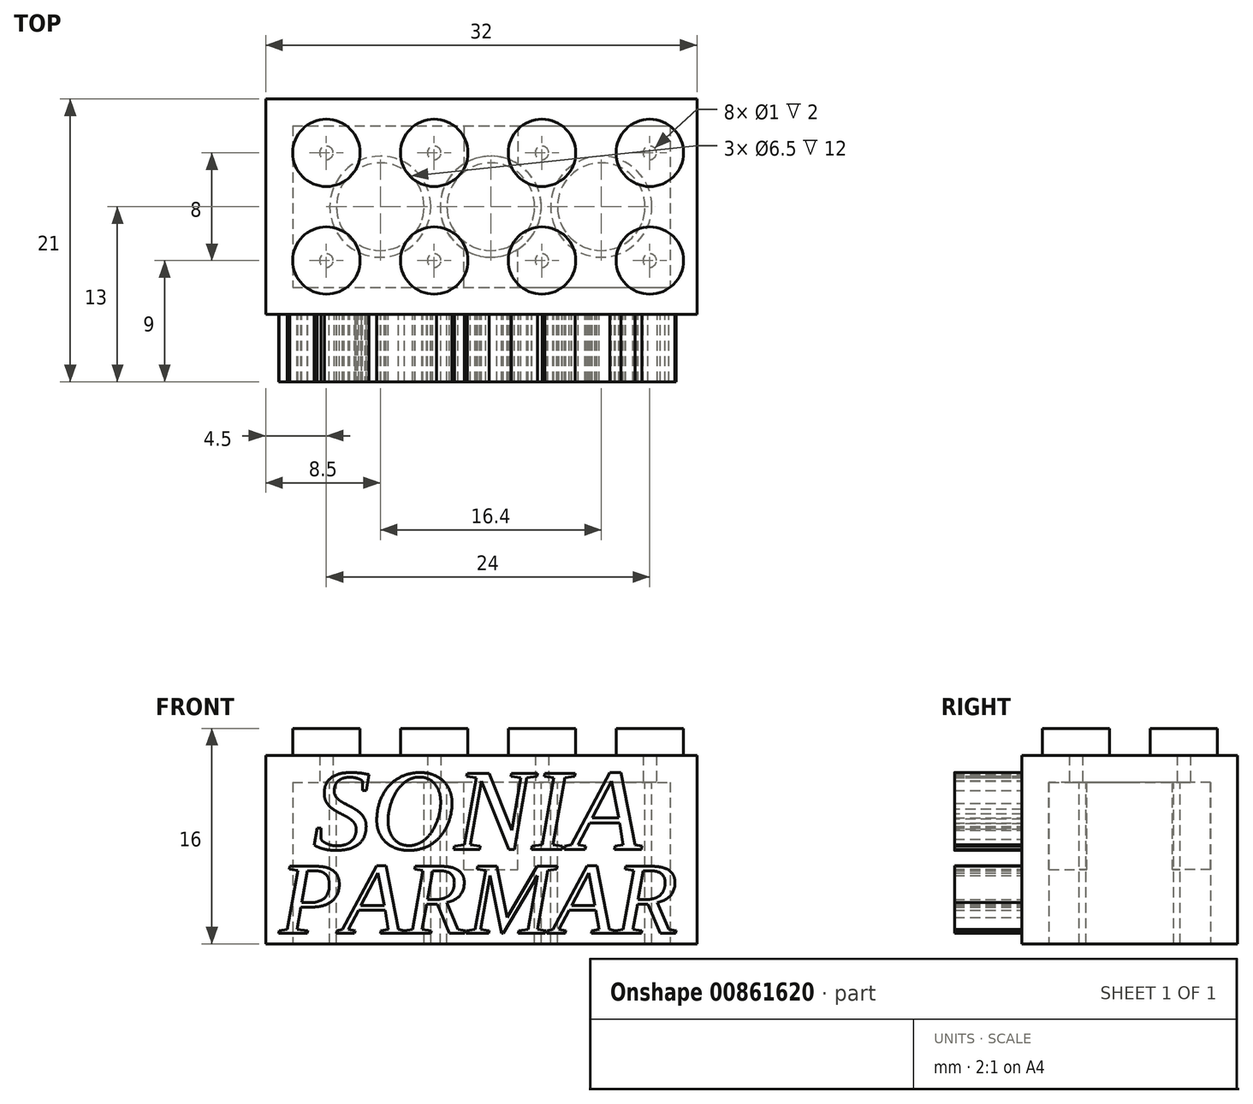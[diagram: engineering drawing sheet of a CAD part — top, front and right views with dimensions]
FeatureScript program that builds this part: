
annotation { "Feature Type Name" : "Feature", "Feature Type Description" : "" }
export const myFeature = defineFeature(function(context is Context, id is Id, definition is map)
    precondition{}
    {
        {
            var Q0;
            Q0=qCreatedBy(makeId("Top.planeOp"),FACE);
            var sketch = newSketch(context, id + "F0", { "sketchPlane" : qUnion([Q0])});
            skLineSegment(sketch, "E0.bottom", {"start": v(-16, 8) * mm, "end": v(16, 8) * mm});
            skLineSegment(sketch, "E0.top", {"start": v(-16, -8) * mm, "end": v(16, -8) * mm});
            skLineSegment(sketch, "E0.left", {"start": v(-16, 8) * mm, "end": v(-16, -8) * mm});
            skLineSegment(sketch, "E0.right", {"start": v(16, 8) * mm, "end": v(16, -8) * mm});
            skPoint(sketch, "E1", {"position": v(-16, 0) * mm});
            skPoint(sketch, "E2", {"position": v(0, 8) * mm});
            skPoint(sketch, "E3", {"position": v(16, 0) * mm});
            skPoint(sketch, "E4", {"position": v(0, -8) * mm});
            skPoint(sketch, "E5", {"position": v(0, 0) * mm});
            skSolve(sketch);
        }
        {
            var Q0;
            Q0=makeQuery(id+"F0.imprint","IMPRINT",FACE,{"disambiguationData":[TD([[makeQuery(id+"F0.imprint","IMPRINT",EDGE,{"derivedFrom":sQuery(id+"F0.wireOp",EDGE,"E0.bottom")}),-1.0]])]});
            extrude(context, id + "F1", {"entities" : qUnion([Q0]), "depth" : 14 * mm, "offsetDistance" : 25 * mm});
        }
        {
            var Q0;
            Q0=makeQuery(id+"F1.opExtrude","CAP_FACE",FACE,{"disambiguationData":[OSD([sQuery(id+"F0.wireOp",EDGE,"E0.bottom"),sQuery(id+"F0.wireOp",EDGE,"E0.top"),sQuery(id+"F0.wireOp",EDGE,"E0.left"),sQuery(id+"F0.wireOp",EDGE,"E0.right")])],"isStart":false});
            var sketch = newSketch(context, id + "F2", { "sketchPlane" : qUnion([Q0])});
            skCircle(sketch, "E6", {"center": v(-11.5, 4) * mm, "radius": 2.5 * mm});
            skCircle(sketch, "E7.0.1.0", {"center": v(-11.5, -4) * mm, "radius": 2.5 * mm});
            skCircle(sketch, "E7.1.0.0", {"center": v(-3.5, 4) * mm, "radius": 2.5 * mm});
            skCircle(sketch, "E7.1.1.0", {"center": v(-3.5, -4) * mm, "radius": 2.5 * mm});
            skCircle(sketch, "E7.2.0.0", {"center": v(4.5, 4) * mm, "radius": 2.5 * mm});
            skCircle(sketch, "E7.2.1.0", {"center": v(4.5, -4) * mm, "radius": 2.5 * mm});
            skCircle(sketch, "E7.3.0.0", {"center": v(12.5, 4) * mm, "radius": 2.5 * mm});
            skCircle(sketch, "E7.3.1.0", {"center": v(12.5, -4) * mm, "radius": 2.5 * mm});
            skLineSegment(sketch, "E7.direction1", {"start": v(-11.5, 4) * mm, "end": v(-3.5, 4) * mm, "construction": true});
            skLineSegment(sketch, "E7.direction2", {"start": v(-11.5, 4) * mm, "end": v(-11.5, -4) * mm, "construction": true});
            skSolve(sketch);
        }
        {
            var Q0;
            Q0=makeQuery(id+"F2.imprint","IMPRINT",FACE,{"disambiguationData":[TD([[makeQuery(id+"F2.imprint","IMPRINT",EDGE,{"derivedFrom":sQuery(id+"F2.wireOp",EDGE,"E6")}),1.0]])]});
            var Q1;
            Q1=makeQuery(id+"F2.imprint","IMPRINT",FACE,{"disambiguationData":[TD([[makeQuery(id+"F2.imprint","IMPRINT",EDGE,{"derivedFrom":sQuery(id+"F2.wireOp",EDGE,"E7.1.0.0")}),1.0]])]});
            var Q2;
            Q2=makeQuery(id+"F2.imprint","IMPRINT",FACE,{"disambiguationData":[TD([[makeQuery(id+"F2.imprint","IMPRINT",EDGE,{"derivedFrom":sQuery(id+"F2.wireOp",EDGE,"E7.3.0.0")}),1.0]])]});
            var Q3;
            Q3=makeQuery(id+"F2.imprint","IMPRINT",FACE,{"disambiguationData":[TD([[makeQuery(id+"F2.imprint","IMPRINT",EDGE,{"derivedFrom":sQuery(id+"F2.wireOp",EDGE,"E7.3.1.0")}),1.0]])]});
            var Q4;
            Q4=makeQuery(id+"F2.imprint","IMPRINT",FACE,{"disambiguationData":[TD([[makeQuery(id+"F2.imprint","IMPRINT",EDGE,{"derivedFrom":sQuery(id+"F2.wireOp",EDGE,"E7.2.1.0")}),1.0]])]});
            var Q5;
            Q5=makeQuery(id+"F2.imprint","IMPRINT",FACE,{"disambiguationData":[TD([[makeQuery(id+"F2.imprint","IMPRINT",EDGE,{"derivedFrom":sQuery(id+"F2.wireOp",EDGE,"E7.1.1.0")}),1.0]])]});
            var Q6;
            Q6=makeQuery(id+"F2.imprint","IMPRINT",FACE,{"disambiguationData":[TD([[makeQuery(id+"F2.imprint","IMPRINT",EDGE,{"derivedFrom":sQuery(id+"F2.wireOp",EDGE,"E7.0.1.0")}),1.0]])]});
            var Q7;
            Q7=makeQuery(id+"F2.imprint","IMPRINT",FACE,{"disambiguationData":[TD([[makeQuery(id+"F2.imprint","IMPRINT",EDGE,{"derivedFrom":sQuery(id+"F2.wireOp",EDGE,"E7.2.0.0")}),1.0]])]});
            extrude(context, id + "F3", {"entities" : qUnion([Q0, Q1, Q2, Q3, Q4, Q5, Q6, Q7]), "operationType" : NewBodyOperationType.ADD, "depth" : 2 * mm, "offsetDistance" : 25 * mm});
        }
        {
            var Q0;
            Q0=makeQuery(id+"F1.opExtrude","CAP_FACE",FACE,{"disambiguationData":[OSD([sQuery(id+"F0.wireOp",EDGE,"E0.bottom"),sQuery(id+"F0.wireOp",EDGE,"E0.top"),sQuery(id+"F0.wireOp",EDGE,"E0.left"),sQuery(id+"F0.wireOp",EDGE,"E0.right")])],"isStart":true});
            shell(context, id + "F4", {"entities" : qUnion([Q0]), "thickness" : 2 * mm});
        }
        {
            var Q0;
            Q0=makeQuery(id+"F4.opShell","OFFSET_FACE",FACE,{"disambiguationData":[OSD([sQuery(id+"F0.wireOp",EDGE,"E0.bottom"),sQuery(id+"F0.wireOp",EDGE,"E0.top"),sQuery(id+"F0.wireOp",EDGE,"E0.left"),sQuery(id+"F0.wireOp",EDGE,"E0.right")])]});
            var sketch = newSketch(context, id + "F5", { "sketchPlane" : qUnion([Q0])});
            skCircle(sketch, "E8", {"center": v(-7.5, 0) * mm, "radius": 3.75 * mm});
            skLineSegment(sketch, "E9", {"start": v(-11.5, 4) * mm, "end": v(-11.5, -4) * mm, "construction": true});
            skLineSegment(sketch, "E10", {"start": v(-11.5, 4) * mm, "end": v(-3.5, 4) * mm, "construction": true});
            skPoint(sketch, "E11", {"position": v(-11.5, 0) * mm});
            skPoint(sketch, "E12", {"position": v(-7.5, 4) * mm});
            skCircle(sketch, "E13", {"center": v(-7.5, 0) * mm, "radius": 3.25 * mm});
            skCircle(sketch, "E14.1.0.0", {"center": v(0.7, 0) * mm, "radius": 3.75 * mm});
            skCircle(sketch, "E14.1.0.1", {"center": v(0.7, 0) * mm, "radius": 3.25 * mm});
            skCircle(sketch, "E14.2.0.0", {"center": v(8.9, 0) * mm, "radius": 3.75 * mm});
            skCircle(sketch, "E14.2.0.1", {"center": v(8.9, 0) * mm, "radius": 3.25 * mm});
            skLineSegment(sketch, "E14.direction1", {"start": v(-7.5, 0) * mm, "end": v(0.7, 0) * mm, "construction": true});
            skSolve(sketch);
        }
        {
            var Q0;
            Q0=makeQuery(id+"F5.imprint","IMPRINT",FACE,{"disambiguationData":[TD([[makeQuery(id+"F5.imprint","IMPRINT",EDGE,{"derivedFrom":sQuery(id+"F5.wireOp",EDGE,"E8")}),1.0]])]});
            var Q1;
            Q1=makeQuery(id+"F5.imprint","IMPRINT",FACE,{"disambiguationData":[TD([[makeQuery(id+"F5.imprint","IMPRINT",EDGE,{"derivedFrom":sQuery(id+"F5.wireOp",EDGE,"E14.1.0.0")}),1.0]])]});
            var Q2;
            Q2=makeQuery(id+"F5.imprint","IMPRINT",FACE,{"disambiguationData":[TD([[makeQuery(id+"F5.imprint","IMPRINT",EDGE,{"derivedFrom":sQuery(id+"F5.wireOp",EDGE,"E14.2.0.0")}),1.0]])]});
            var Q3;
            Q3=makeQuery(id+"F1.opExtrude","CAP_FACE",FACE,{"disambiguationData":[OSD([sQuery(id+"F0.wireOp",EDGE,"E0.bottom"),sQuery(id+"F0.wireOp",EDGE,"E0.top"),sQuery(id+"F0.wireOp",EDGE,"E0.left"),sQuery(id+"F0.wireOp",EDGE,"E0.right")])],"isStart":true});
            extrude(context, id + "F6", {"entities" : qUnion([Q0, Q1, Q2]), "operationType" : NewBodyOperationType.ADD, "endBound" : BoundingType.UP_TO_SURFACE, "depth" : 12 * mm, "endBoundEntityFace" : qUnion([Q3]), "offsetDistance" : 25 * mm});
        }
        {
            var Q0;
            {var subQ4=sQuery(id+"F0.wireOp",EDGE,"E0.bottom");var subQ6=sQuery(id+"F0.wireOp",EDGE,"E0.top");var subQ7=sQuery(id+"F0.wireOp",EDGE,"E0.left");var subQ9=sQuery(id+"F0.wireOp",EDGE,"E0.right");Q0=makeQuery(id+"F6.boolean.opBoolean","SPLIT",FACE,{"disambiguationData":[TD([makeQuery(id+"F4.opShell","OFFSET_FACE",FACE,{"disambiguationData":[OSD([subQ4])]})])],"derivedFrom":makeQuery(id+"F4.opShell","OFFSET_FACE",FACE,{"disambiguationData":[OSD([subQ4,subQ6,subQ7,subQ9])]})});}
            var sketch = newSketch(context, id + "F7", { "sketchPlane" : qUnion([Q0])});
            skCircle(sketch, "E15.0", {"center": v(0.7, 0) * mm, "radius": 3.75 * mm});
            skLineSegment(sketch, "E16", {"start": v(0.7, 9.8) * mm, "end": v(0.7, -11.34) * mm, "construction": true});
            skLineSegment(sketch, "E17", {"start": v(-1.3, 6) * mm, "end": v(-1.3, 3.17) * mm});
            skLineSegment(sketch, "E18", {"start": v(2.7, 6) * mm, "end": v(2.7, 3.17) * mm});
            skLineSegment(sketch, "E19", {"start": v(-1.3, -6) * mm, "end": v(-1.3, -3.17) * mm});
            skLineSegment(sketch, "E20", {"start": v(2.7, -6) * mm, "end": v(2.7, -3.17) * mm});
            skSolve(sketch);
        }
        {
            var Q0;
            {var subQ0=sQuery(id+"F7.wireOp",EDGE,"E17");Q0=makeQuery(id+"F7.imprint","IMPRINT",FACE,{"disambiguationData":[TD([[makeQuery(id+"F7.imprint","IMPRINT",EDGE,{"derivedFrom":subQ0}),1.0]])]});}
            var Q1;
            {var subQ0=sQuery(id+"F7.wireOp",EDGE,"E19");Q1=makeQuery(id+"F7.imprint","IMPRINT",FACE,{"disambiguationData":[TD([[makeQuery(id+"F7.imprint","IMPRINT",EDGE,{"derivedFrom":subQ0}),-1.0]])]});}
            extrude(context, id + "F8", {"entities" : qUnion([Q0, Q1]), "operationType" : NewBodyOperationType.ADD, "depth" : 6.5 * mm, "offsetDistance" : 25 * mm});
        }
        {
            var Q0;
            Q0=makeQuery(id+"F1.opExtrude","SWEPT_FACE",FACE,{"disambiguationData":[OSD([sQuery(id+"F0.wireOp",EDGE,"E0.top")])]});
            var sketch = newSketch(context, id + "F9", { "sketchPlane" : qUnion([Q0])});
            skText(sketch, "E21", { "text": "SONIA", "fontName": "Tinos-Italic.ttf"});
            const initialGuessF9  = {"E21": [-0.0125, 0.00702, 1, 0, 0.0062]};
            skSetInitialGuess(sketch, initialGuessF9);
            skSolve(sketch);
        }
        {
            var Q0;
            Q0=makeQuery(id+"F9.imprint","IMPRINT",FACE,{"disambiguationData":[TD([[makeQuery(id+"F9.imprint","IMPRINT",EDGE,{"derivedFrom":sQuery(id+"F9.wireOp",EDGE,"E21.sketch_text.stroke-0")}),1.0]])]});
            var sketch = newSketch(context, id + "F10", { "sketchPlane" : qUnion([Q0])});
            skText(sketch, "E22", { "text": "PARMAR", "fontName": "Tinos-Italic.ttf"});
            const initialGuessF10  = {"E22": [-0.015, 0.00077, 1, 0, 0.00548]};
            skSetInitialGuess(sketch, initialGuessF10);
            skSolve(sketch);
        }
        {
            var Q0;
            Q0 = qSketchRegion(id + "F9", true);
            extrude(context, id + "F11", {"entities" : qUnion([Q0]), "operationType" : NewBodyOperationType.ADD, "depth" : 5 * mm, "offsetDistance" : 25 * mm});
        }
        {
            var Q0;
            Q0 = qSketchRegion(id + "F10", true);
            extrude(context, id + "F12", {"entities" : qUnion([Q0]), "operationType" : NewBodyOperationType.ADD, "depth" : 5 * mm, "offsetDistance" : 25 * mm});
        }
    });
